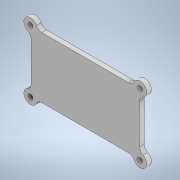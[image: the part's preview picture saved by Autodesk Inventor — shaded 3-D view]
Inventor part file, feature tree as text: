
AUTODESK INVENTOR PART (.ipt)
format: ipt  version: 2020 (Build 240168000, 168)  size: 168,448 bytes
history: native  units: in
note: dims shown in document units (in); Inventor stores cm internally (conversion verified against a paired STEP export)
features: extrude x3, sketch x3, fillet x2, plane x2, mirror x2, projected_geometry x1
ambient origin geometry x8: Origin, YZ Plane, XZ Plane, XY Plane, X Axis, Y Axis, Z Axis, Center Point
bodies: Solid1 (feature_tree)
feature tree (13):
  extrude  "Extrusion1"  Depth=1.04in
  extrude  "Extrusion2"  Depth=0.1in TaperAngle=0.0deg
  fillet  "Fillet1"  Radius=0.125in
  extrude  "Extrusion3"  Depth=0.1in TaperAngle=0.0deg
  plane  "Work Plane1"
  plane  "Work Plane2"
  mirror  "Mirror1"
  mirror  "Mirror2"
  fillet  "Fillet3"  Radius=0.125in
  sketch  "Sketch1"  dims[d0=2.05in d1=1.04in]
  sketch  "Sketch2"  dims[d2=0.1in d3=0.0in d5=0.1in d6=0.0in d11=0.125in]
  projected_geometry  "Projected Loop1"
  sketch  "Sketch4"  dims[d12=0.1094in d14=0.1in d15=0.0in d18=0.125in d19=0.125in d20=0.125in d21=0.125in d23=0.14in d24=0.125in d25=1.29in d26=2.3in]
